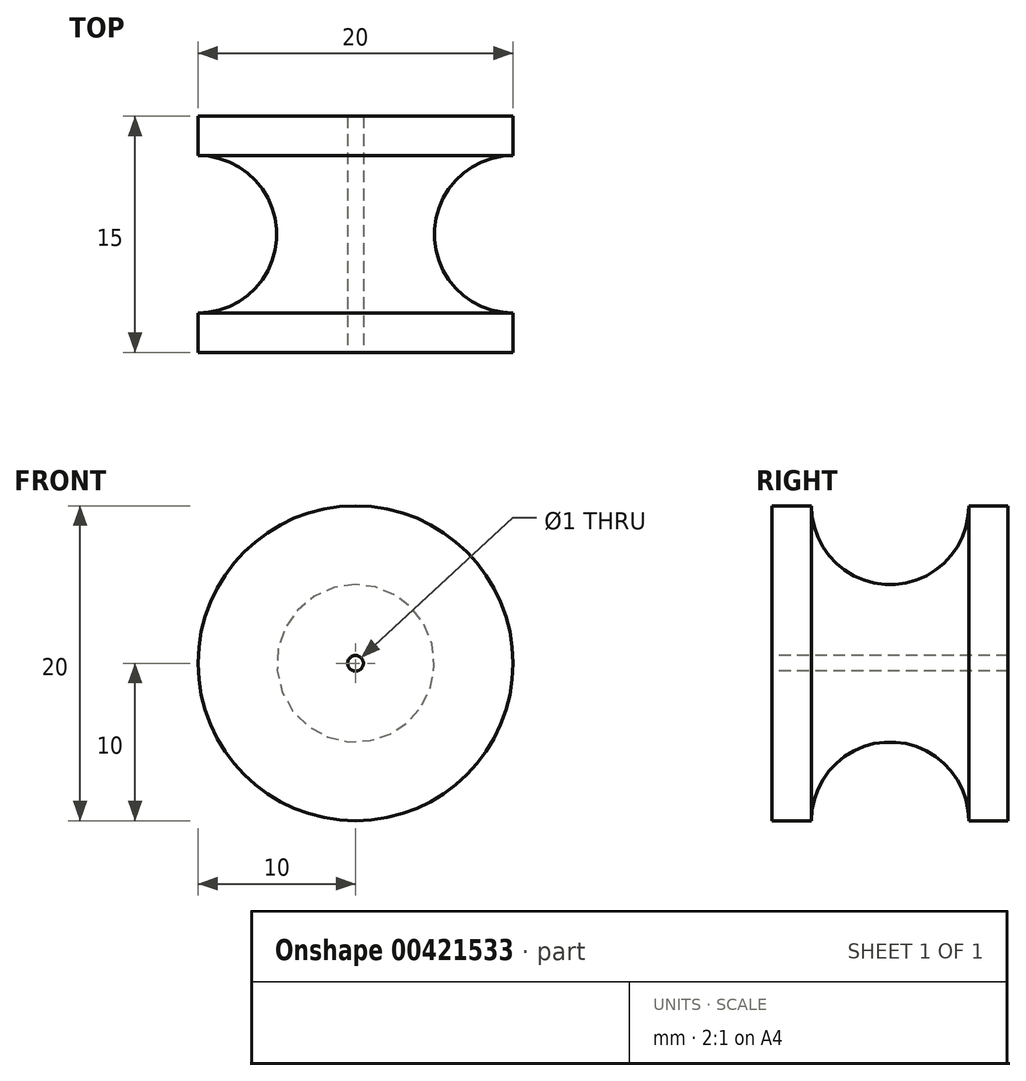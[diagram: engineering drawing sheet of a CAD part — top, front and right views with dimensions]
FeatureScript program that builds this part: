
annotation { "Feature Type Name" : "Feature", "Feature Type Description" : "" }
export const myFeature = defineFeature(function(context is Context, id is Id, definition is map)
    precondition{}
    {
        {
            var Q0;
            Q0=qCreatedBy(makeId("Front.planeOp"),FACE);
            var sketch = newSketch(context, id + "F0", { "sketchPlane" : qUnion([Q0])});
            skCircle(sketch, "E0", {"center": v(0, 0) * mm, "radius": 10 * mm});
            skSolve(sketch);
        }
        {
            var Q0;
            Q0 = qSketchRegion(id + "F0", true);
            extrude(context, id + "F1", {"entities" : qUnion([Q0]), "endBound" : BoundingType.SYMMETRIC, "depth" : 15 * mm});
        }
        {
            var Q0;
            Q0=qCreatedBy(makeId("Right.planeOp"),FACE);
            var sketch = newSketch(context, id + "F2", { "sketchPlane" : qUnion([Q0])});
            skLineSegment(sketch, "E1.bottom", {"start": v(-7.5, 10) * mm, "end": v(7.5, 10) * mm, "construction": true});
            skLineSegment(sketch, "E1.top", {"start": v(-7.5, -10) * mm, "end": v(7.5, -10) * mm, "construction": true});
            skLineSegment(sketch, "E1.left", {"start": v(-7.5, 10) * mm, "end": v(-7.5, -10) * mm, "construction": true});
            skLineSegment(sketch, "E1.right", {"start": v(7.5, 10) * mm, "end": v(7.5, -10) * mm, "construction": true});
            skPoint(sketch, "E1.middle", {"position": v(0, 0) * mm});
            skArc(sketch, "E2", {"start": v(-5, 10) * mm, "mid": v(0, 5) * mm, "end": v(5, 10) * mm});
            skLineSegment(sketch, "E3", {"start": v(-5, 10) * mm, "end": v(5, 10) * mm});
            skSolve(sketch);
        }
        {
            var Q0;
            Q0=qCreatedBy(makeId("Right.planeOp"),FACE);
            var sketch = newSketch(context, id + "F3", { "sketchPlane" : qUnion([Q0])});
            skLineSegment(sketch, "E4", {"start": v(-15.57, 0) * mm, "end": v(3.9, 0) * mm});
            skSolve(sketch);
        }
        {
            var Q0;
            Q0 = qSketchRegion(id + "F2", true);
            var Q1;
            Q1=sQuery(id+"F3.wireOp",EDGE,"E4");
            revolve(context, id + "F4", {"operationType" : NewBodyOperationType.REMOVE, "entities" : qUnion([Q0]), "axis" : qUnion([Q1]), "revolveType" : RevolveType.FULL, "oppositeDirection" : true});
        }
        {
            var Q0;
            Q0=makeQuery(id+"F1.opExtrude","CAP_FACE",FACE,{"disambiguationData":[OSD([sQuery(id+"F0.wireOp",EDGE,"E0")])],"isStart":false});
            var sketch = newSketch(context, id + "F5", { "sketchPlane" : qUnion([Q0])});
            skCircle(sketch, "E5", {"center": v(0, 0) * mm, "radius": 0.5 * mm});
            skSolve(sketch);
        }
        {
            var Q0;
            Q0 = qSketchRegion(id + "F5", true);
            extrude(context, id + "F6", {"entities" : qUnion([Q0]), "operationType" : NewBodyOperationType.REMOVE, "endBound" : BoundingType.THROUGH_ALL, "oppositeDirection" : true, "depth" : 25 * mm});
        }
    });
